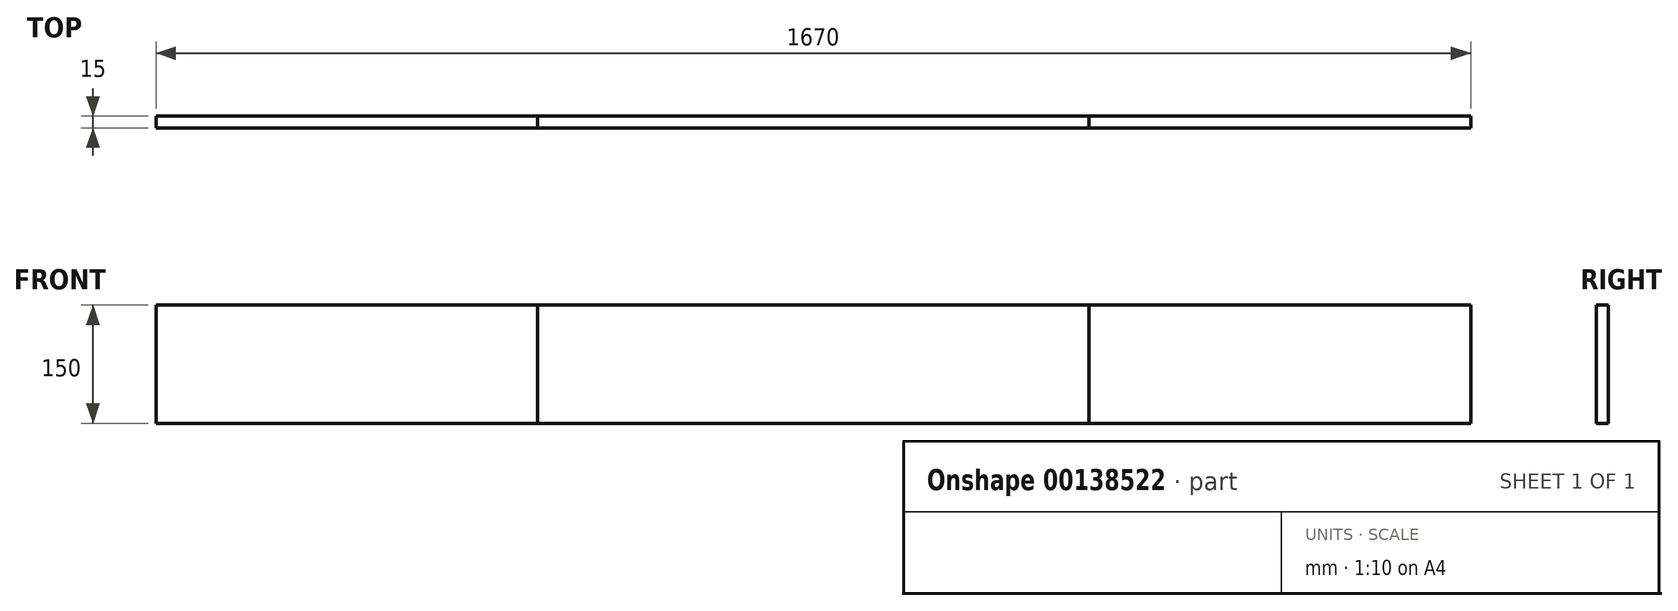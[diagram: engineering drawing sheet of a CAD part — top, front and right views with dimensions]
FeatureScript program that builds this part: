
annotation { "Feature Type Name" : "Feature", "Feature Type Description" : "" }
export const myFeature = defineFeature(function(context is Context, id is Id, definition is map)
    precondition{}
    {
        {
            var Q0;
            Q0=qCreatedBy(makeId("Right.planeOp"),FACE);
            var sketch = newSketch(context, id + "F0", { "sketchPlane" : qUnion([Q0])});
            skLineSegment(sketch, "E0.bottom", {"start": v(7.5, -75) * mm, "end": v(-7.5, -75) * mm});
            skLineSegment(sketch, "E0.top", {"start": v(7.5, 75) * mm, "end": v(-7.5, 75) * mm});
            skLineSegment(sketch, "E0.left", {"start": v(7.5, -75) * mm, "end": v(7.5, 75) * mm});
            skLineSegment(sketch, "E0.right", {"start": v(-7.5, -75) * mm, "end": v(-7.5, 75) * mm});
            skPoint(sketch, "E0.middle", {"position": v(0, 0) * mm});
            skSolve(sketch);
        }
        {
            var Q0;
            Q0=makeQuery(id+"F0.imprint","IMPRINT",FACE,{"disambiguationData":[TD([[makeQuery(id+"F0.imprint","IMPRINT",EDGE,{"derivedFrom":sQuery(id+"F0.wireOp",EDGE,"E0.bottom")}),-1.0]])]});
            extrude(context, id + "F1", {"entities" : qUnion([Q0]), "endBound" : BoundingType.SYMMETRIC, "depth" : 1670 * mm});
        }
        {
            var Q0;
            Q0 = qSketchRegion(id + "F0", true);
            extrude(context, id + "F2", {"entities" : qUnion([Q0]), "endBound" : BoundingType.SYMMETRIC, "depth" : 700 * mm});
        }
    });
